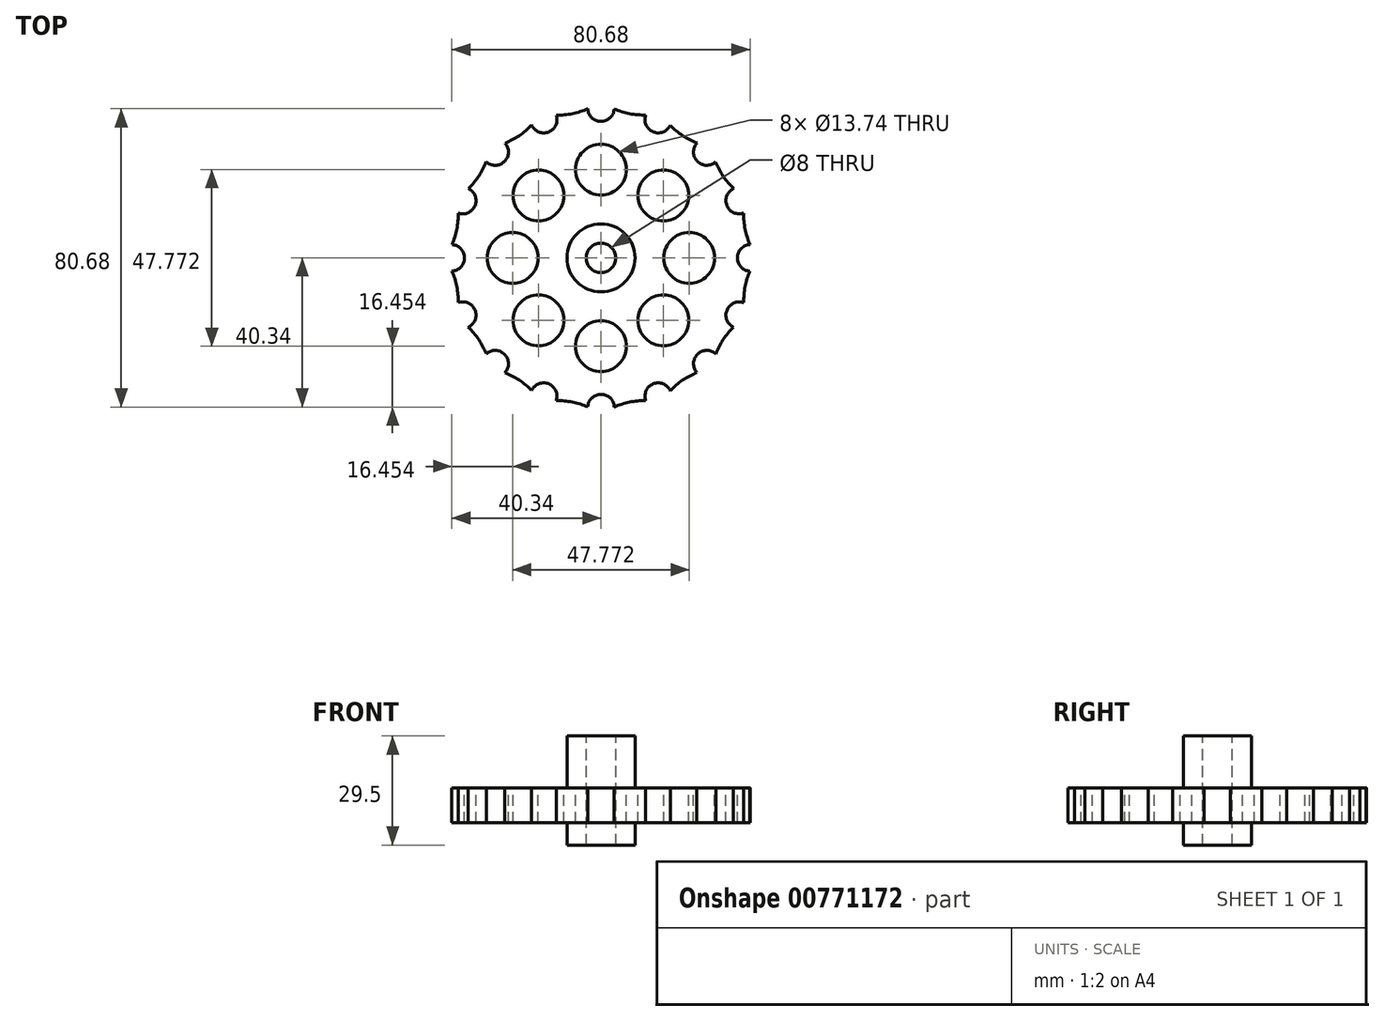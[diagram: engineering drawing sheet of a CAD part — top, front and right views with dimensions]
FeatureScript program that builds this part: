
annotation { "Feature Type Name" : "Feature", "Feature Type Description" : "" }
export const myFeature = defineFeature(function(context is Context, id is Id, definition is map)
    precondition{}
    {
        {
            var Q0;
            Q0=qCreatedBy(makeId("Front.planeOp"),FACE);
            var sketch = newSketch(context, id + "F0", { "sketchPlane" : qUnion([Q0])});
            skLineSegment(sketch, "E0", {"start": v(4, 29.5) * mm, "end": v(4, 0) * mm});
            skLineSegment(sketch, "E1", {"start": v(4, 0) * mm, "end": v(9.2, 0) * mm});
            skLineSegment(sketch, "E2", {"start": v(9.2, 0) * mm, "end": v(9.2, 6) * mm});
            skLineSegment(sketch, "E3", {"start": v(9.2, 6) * mm, "end": v(40.5, 6) * mm});
            skLineSegment(sketch, "E4", {"start": v(40.5, 6) * mm, "end": v(40.5, 15.5) * mm});
            skLineSegment(sketch, "E5", {"start": v(40.5, 15.5) * mm, "end": v(9.2, 15.5) * mm});
            skLineSegment(sketch, "E6", {"start": v(9.2, 15.5) * mm, "end": v(9.2, 29.5) * mm});
            skLineSegment(sketch, "E7", {"start": v(9.2, 29.5) * mm, "end": v(4, 29.5) * mm});
            skLineSegment(sketch, "E8", {"start": v(0, 75.26) * mm, "end": v(0, -74.89) * mm});
            skSolve(sketch);
        }
        {
            var Q0;
            Q0=makeQuery(id+"F0.imprint","IMPRINT",FACE,{"disambiguationData":[TD([[makeQuery(id+"F0.imprint","IMPRINT",EDGE,{"derivedFrom":sQuery(id+"F0.wireOp",EDGE,"E0")}),1.0]])]});
            var Q1;
            Q1=sQuery(id+"F0.wireOp",EDGE,"E8");
            revolve(context, id + "F1", {"surfaceOperationType" : NewSurfaceOperationType.NEW, "entities" : qUnion([Q0]), "axis" : qUnion([Q1]), "revolveType" : RevolveType.FULL});
        }
        {
            var Q0;
            Q0=makeQuery(id+"F1.opRevolve","SWEPT_FACE",FACE,{"disambiguationData":[OSD([sQuery(id+"F0.wireOp",EDGE,"E5")])]});
            var sketch = newSketch(context, id + "F2", { "sketchPlane" : qUnion([Q0])});
            skCircle(sketch, "E9", {"center": v(40.5, 0) * mm, "radius": 3.6 * mm});
            skCircle(sketch, "E10.1.0", {"center": v(37.42, 15.5) * mm, "radius": 3.6 * mm});
            skCircle(sketch, "E10.2.0", {"center": v(28.64, 28.64) * mm, "radius": 3.6 * mm});
            skCircle(sketch, "E10.3.0", {"center": v(15.5, 37.42) * mm, "radius": 3.6 * mm});
            skCircle(sketch, "E10.4.0", {"center": v(0, 40.5) * mm, "radius": 3.6 * mm});
            skCircle(sketch, "E10.5.0", {"center": v(-15.5, 37.42) * mm, "radius": 3.6 * mm});
            skCircle(sketch, "E10.6.0", {"center": v(-28.64, 28.64) * mm, "radius": 3.6 * mm});
            skCircle(sketch, "E10.7.0", {"center": v(-37.42, 15.5) * mm, "radius": 3.6 * mm});
            skCircle(sketch, "E10.8.0", {"center": v(-40.5, 0) * mm, "radius": 3.6 * mm});
            skCircle(sketch, "E10.9.0", {"center": v(-37.42, -15.5) * mm, "radius": 3.6 * mm});
            skCircle(sketch, "E10.10.0", {"center": v(-28.64, -28.64) * mm, "radius": 3.6 * mm});
            skCircle(sketch, "E10.11.0", {"center": v(-15.5, -37.42) * mm, "radius": 3.6 * mm});
            skCircle(sketch, "E10.12.0", {"center": v(0, -40.5) * mm, "radius": 3.6 * mm});
            skCircle(sketch, "E10.13.0", {"center": v(15.5, -37.42) * mm, "radius": 3.6 * mm});
            skCircle(sketch, "E10.14.0", {"center": v(28.64, -28.64) * mm, "radius": 3.6 * mm});
            skCircle(sketch, "E10.15.0", {"center": v(37.42, -15.5) * mm, "radius": 3.6 * mm});
            skPoint(sketch, "E10.center", {"position": v(0, 0) * mm});
            skArc(sketch, "E11", {"start": v(38.6, 12.1) * mm, "mid": v(39.02, 7.76) * mm, "end": v(40.34, 3.6) * mm});
            skArc(sketch, "E12.1.0", {"start": v(31.04, 25.96) * mm, "mid": v(33.08, 22.1) * mm, "end": v(35.9, 18.76) * mm});
            skArc(sketch, "E12.2.0", {"start": v(18.74, 35.86) * mm, "mid": v(22.1, 33.07) * mm, "end": v(25.98, 31.07) * mm});
            skArc(sketch, "E12.3.0", {"start": v(3.6, 40.3) * mm, "mid": v(7.77, 39.01) * mm, "end": v(12.11, 38.65) * mm});
            skArc(sketch, "E12.4.0", {"start": v(-12.1, 38.6) * mm, "mid": v(-7.76, 39.02) * mm, "end": v(-3.6, 40.34) * mm});
            skArc(sketch, "E12.5.0", {"start": v(-25.96, 31.04) * mm, "mid": v(-22.1, 33.08) * mm, "end": v(-18.76, 35.9) * mm});
            skArc(sketch, "E12.6.0", {"start": v(-35.86, 18.74) * mm, "mid": v(-33.07, 22.1) * mm, "end": v(-31.07, 25.98) * mm});
            skArc(sketch, "E12.7.0", {"start": v(-40.3, 3.6) * mm, "mid": v(-39.01, 7.77) * mm, "end": v(-38.65, 12.11) * mm});
            skArc(sketch, "E12.8.0", {"start": v(-38.6, -12.1) * mm, "mid": v(-39.02, -7.76) * mm, "end": v(-40.34, -3.6) * mm});
            skArc(sketch, "E12.9.0", {"start": v(-31.04, -25.96) * mm, "mid": v(-33.08, -22.1) * mm, "end": v(-35.9, -18.76) * mm});
            skArc(sketch, "E12.10.0", {"start": v(-18.74, -35.86) * mm, "mid": v(-22.1, -33.07) * mm, "end": v(-25.98, -31.07) * mm});
            skArc(sketch, "E12.11.0", {"start": v(-3.6, -40.3) * mm, "mid": v(-7.77, -39.01) * mm, "end": v(-12.11, -38.65) * mm});
            skArc(sketch, "E12.12.0", {"start": v(12.1, -38.6) * mm, "mid": v(7.76, -39.02) * mm, "end": v(3.6, -40.34) * mm});
            skArc(sketch, "E12.13.0", {"start": v(25.96, -31.04) * mm, "mid": v(22.1, -33.08) * mm, "end": v(18.76, -35.9) * mm});
            skArc(sketch, "E12.14.0", {"start": v(35.86, -18.74) * mm, "mid": v(33.07, -22.1) * mm, "end": v(31.07, -25.98) * mm});
            skArc(sketch, "E12.15.0", {"start": v(40.3, -3.6) * mm, "mid": v(39.01, -7.77) * mm, "end": v(38.65, -12.11) * mm});
            skSolve(sketch);
        }
        {
            var Q0;
            {var subQ0=sQuery(id+"F2.wireOp",EDGE,"E9");var subQ1=makeQuery(id+"F1.opRevolve","SWEPT_EDGE",EDGE,{"disambiguationData":[OSD([sQuery(id+"F0.wireOp",EDGE,"E4"),sQuery(id+"F0.wireOp",EDGE,"E5")])]});var subQ3=makeQuery(id+"F2.imprint","INTERSECT",VERTEX,{"derivedFrom":[subQ1,subQ0]});Q0=makeQuery(id+"F2.imprint","IMPRINT",FACE,{"disambiguationData":[TD([[makeQuery(id+"F2.imprint","IMPRINT",EDGE,{"disambiguationData":[TD([[subQ3,-1.0]])],"derivedFrom":subQ0}),1.0]])]});}
            var Q1;
            {var subQ0=sQuery(id+"F2.wireOp",EDGE,"E10.1.0");var subQ1=makeQuery(id+"F1.opRevolve","SWEPT_EDGE",EDGE,{"disambiguationData":[OSD([sQuery(id+"F0.wireOp",EDGE,"E4"),sQuery(id+"F0.wireOp",EDGE,"E5")])]});var subQ3=makeQuery(id+"F2.imprint","INTERSECT",VERTEX,{"derivedFrom":[subQ1,subQ0]});Q1=makeQuery(id+"F2.imprint","IMPRINT",FACE,{"disambiguationData":[TD([[makeQuery(id+"F2.imprint","IMPRINT",EDGE,{"disambiguationData":[TD([[subQ3,-1.0]])],"derivedFrom":subQ0}),1.0]])]});}
            var Q2;
            {var subQ0=sQuery(id+"F2.wireOp",EDGE,"E10.2.0");var subQ1=makeQuery(id+"F1.opRevolve","SWEPT_EDGE",EDGE,{"disambiguationData":[OSD([sQuery(id+"F0.wireOp",EDGE,"E4"),sQuery(id+"F0.wireOp",EDGE,"E5")])]});var subQ3=makeQuery(id+"F2.imprint","INTERSECT",VERTEX,{"derivedFrom":[subQ1,subQ0]});Q2=makeQuery(id+"F2.imprint","IMPRINT",FACE,{"disambiguationData":[TD([[makeQuery(id+"F2.imprint","IMPRINT",EDGE,{"disambiguationData":[TD([[subQ3,-1.0]])],"derivedFrom":subQ0}),1.0]])]});}
            var Q3;
            {var subQ0=sQuery(id+"F2.wireOp",EDGE,"E10.3.0");var subQ1=makeQuery(id+"F1.opRevolve","SWEPT_EDGE",EDGE,{"disambiguationData":[OSD([sQuery(id+"F0.wireOp",EDGE,"E4"),sQuery(id+"F0.wireOp",EDGE,"E5")])]});var subQ3=makeQuery(id+"F2.imprint","INTERSECT",VERTEX,{"derivedFrom":[subQ1,subQ0]});Q3=makeQuery(id+"F2.imprint","IMPRINT",FACE,{"disambiguationData":[TD([[makeQuery(id+"F2.imprint","IMPRINT",EDGE,{"disambiguationData":[TD([[subQ3,-1.0]])],"derivedFrom":subQ0}),1.0]])]});}
            var Q4;
            {var subQ0=sQuery(id+"F2.wireOp",EDGE,"E10.4.0");var subQ1=makeQuery(id+"F1.opRevolve","SWEPT_EDGE",EDGE,{"disambiguationData":[OSD([sQuery(id+"F0.wireOp",EDGE,"E4"),sQuery(id+"F0.wireOp",EDGE,"E5")])]});var subQ3=makeQuery(id+"F2.imprint","INTERSECT",VERTEX,{"derivedFrom":[subQ1,subQ0]});Q4=makeQuery(id+"F2.imprint","IMPRINT",FACE,{"disambiguationData":[TD([[makeQuery(id+"F2.imprint","IMPRINT",EDGE,{"disambiguationData":[TD([[subQ3,-1.0]])],"derivedFrom":subQ0}),1.0]])]});}
            var Q5;
            {var subQ0=sQuery(id+"F2.wireOp",EDGE,"E10.5.0");var subQ1=makeQuery(id+"F1.opRevolve","SWEPT_EDGE",EDGE,{"disambiguationData":[OSD([sQuery(id+"F0.wireOp",EDGE,"E4"),sQuery(id+"F0.wireOp",EDGE,"E5")])]});var subQ3=makeQuery(id+"F2.imprint","INTERSECT",VERTEX,{"derivedFrom":[subQ1,subQ0]});Q5=makeQuery(id+"F2.imprint","IMPRINT",FACE,{"disambiguationData":[TD([[makeQuery(id+"F2.imprint","IMPRINT",EDGE,{"disambiguationData":[TD([[subQ3,-1.0]])],"derivedFrom":subQ0}),1.0]])]});}
            var Q6;
            {var subQ0=sQuery(id+"F2.wireOp",EDGE,"E10.6.0");var subQ1=makeQuery(id+"F1.opRevolve","SWEPT_EDGE",EDGE,{"disambiguationData":[OSD([sQuery(id+"F0.wireOp",EDGE,"E4"),sQuery(id+"F0.wireOp",EDGE,"E5")])]});var subQ3=makeQuery(id+"F2.imprint","INTERSECT",VERTEX,{"derivedFrom":[subQ1,subQ0]});Q6=makeQuery(id+"F2.imprint","IMPRINT",FACE,{"disambiguationData":[TD([[makeQuery(id+"F2.imprint","IMPRINT",EDGE,{"disambiguationData":[TD([[subQ3,-1.0]])],"derivedFrom":subQ0}),1.0]])]});}
            var Q7;
            {var subQ0=sQuery(id+"F2.wireOp",EDGE,"E10.7.0");var subQ1=makeQuery(id+"F1.opRevolve","SWEPT_EDGE",EDGE,{"disambiguationData":[OSD([sQuery(id+"F0.wireOp",EDGE,"E4"),sQuery(id+"F0.wireOp",EDGE,"E5")])]});var subQ3=makeQuery(id+"F2.imprint","INTERSECT",VERTEX,{"derivedFrom":[subQ1,subQ0]});Q7=makeQuery(id+"F2.imprint","IMPRINT",FACE,{"disambiguationData":[TD([[makeQuery(id+"F2.imprint","IMPRINT",EDGE,{"disambiguationData":[TD([[subQ3,-1.0]])],"derivedFrom":subQ0}),1.0]])]});}
            var Q8;
            {var subQ0=sQuery(id+"F2.wireOp",EDGE,"E10.8.0");var subQ1=makeQuery(id+"F1.opRevolve","SWEPT_EDGE",EDGE,{"disambiguationData":[OSD([sQuery(id+"F0.wireOp",EDGE,"E4"),sQuery(id+"F0.wireOp",EDGE,"E5")])]});var subQ3=makeQuery(id+"F2.imprint","INTERSECT",VERTEX,{"derivedFrom":[subQ1,subQ0]});Q8=makeQuery(id+"F2.imprint","IMPRINT",FACE,{"disambiguationData":[TD([[makeQuery(id+"F2.imprint","IMPRINT",EDGE,{"disambiguationData":[TD([[subQ3,-1.0]])],"derivedFrom":subQ0}),1.0]])]});}
            var Q9;
            {var subQ0=sQuery(id+"F2.wireOp",EDGE,"E10.9.0");var subQ1=makeQuery(id+"F1.opRevolve","SWEPT_EDGE",EDGE,{"disambiguationData":[OSD([sQuery(id+"F0.wireOp",EDGE,"E4"),sQuery(id+"F0.wireOp",EDGE,"E5")])]});var subQ3=makeQuery(id+"F2.imprint","INTERSECT",VERTEX,{"derivedFrom":[subQ1,subQ0]});Q9=makeQuery(id+"F2.imprint","IMPRINT",FACE,{"disambiguationData":[TD([[makeQuery(id+"F2.imprint","IMPRINT",EDGE,{"disambiguationData":[TD([[subQ3,-1.0]])],"derivedFrom":subQ0}),1.0]])]});}
            var Q10;
            {var subQ0=sQuery(id+"F2.wireOp",EDGE,"E10.10.0");var subQ1=makeQuery(id+"F1.opRevolve","SWEPT_EDGE",EDGE,{"disambiguationData":[OSD([sQuery(id+"F0.wireOp",EDGE,"E4"),sQuery(id+"F0.wireOp",EDGE,"E5")])]});var subQ3=makeQuery(id+"F2.imprint","INTERSECT",VERTEX,{"derivedFrom":[subQ1,subQ0]});Q10=makeQuery(id+"F2.imprint","IMPRINT",FACE,{"disambiguationData":[TD([[makeQuery(id+"F2.imprint","IMPRINT",EDGE,{"disambiguationData":[TD([[subQ3,-1.0]])],"derivedFrom":subQ0}),1.0]])]});}
            var Q11;
            {var subQ0=sQuery(id+"F2.wireOp",EDGE,"E10.11.0");var subQ1=makeQuery(id+"F1.opRevolve","SWEPT_EDGE",EDGE,{"disambiguationData":[OSD([sQuery(id+"F0.wireOp",EDGE,"E4"),sQuery(id+"F0.wireOp",EDGE,"E5")])]});var subQ3=makeQuery(id+"F2.imprint","INTERSECT",VERTEX,{"derivedFrom":[subQ1,subQ0]});Q11=makeQuery(id+"F2.imprint","IMPRINT",FACE,{"disambiguationData":[TD([[makeQuery(id+"F2.imprint","IMPRINT",EDGE,{"disambiguationData":[TD([[subQ3,-1.0]])],"derivedFrom":subQ0}),1.0]])]});}
            var Q12;
            {var subQ0=sQuery(id+"F2.wireOp",EDGE,"E10.12.0");var subQ1=makeQuery(id+"F1.opRevolve","SWEPT_EDGE",EDGE,{"disambiguationData":[OSD([sQuery(id+"F0.wireOp",EDGE,"E4"),sQuery(id+"F0.wireOp",EDGE,"E5")])]});var subQ3=makeQuery(id+"F2.imprint","INTERSECT",VERTEX,{"derivedFrom":[subQ1,subQ0]});Q12=makeQuery(id+"F2.imprint","IMPRINT",FACE,{"disambiguationData":[TD([[makeQuery(id+"F2.imprint","IMPRINT",EDGE,{"disambiguationData":[TD([[subQ3,-1.0]])],"derivedFrom":subQ0}),1.0]])]});}
            var Q13;
            {var subQ0=sQuery(id+"F2.wireOp",EDGE,"E10.13.0");var subQ1=makeQuery(id+"F1.opRevolve","SWEPT_EDGE",EDGE,{"disambiguationData":[OSD([sQuery(id+"F0.wireOp",EDGE,"E4"),sQuery(id+"F0.wireOp",EDGE,"E5")])]});var subQ3=makeQuery(id+"F2.imprint","INTERSECT",VERTEX,{"derivedFrom":[subQ1,subQ0]});Q13=makeQuery(id+"F2.imprint","IMPRINT",FACE,{"disambiguationData":[TD([[makeQuery(id+"F2.imprint","IMPRINT",EDGE,{"disambiguationData":[TD([[subQ3,-1.0]])],"derivedFrom":subQ0}),1.0]])]});}
            var Q14;
            {var subQ0=sQuery(id+"F2.wireOp",EDGE,"E10.14.0");var subQ1=makeQuery(id+"F1.opRevolve","SWEPT_EDGE",EDGE,{"disambiguationData":[OSD([sQuery(id+"F0.wireOp",EDGE,"E4"),sQuery(id+"F0.wireOp",EDGE,"E5")])]});var subQ3=makeQuery(id+"F2.imprint","INTERSECT",VERTEX,{"derivedFrom":[subQ1,subQ0]});Q14=makeQuery(id+"F2.imprint","IMPRINT",FACE,{"disambiguationData":[TD([[makeQuery(id+"F2.imprint","IMPRINT",EDGE,{"disambiguationData":[TD([[subQ3,-1.0]])],"derivedFrom":subQ0}),1.0]])]});}
            var Q15;
            {var subQ0=sQuery(id+"F2.wireOp",EDGE,"E10.15.0");var subQ1=makeQuery(id+"F1.opRevolve","SWEPT_EDGE",EDGE,{"disambiguationData":[OSD([sQuery(id+"F0.wireOp",EDGE,"E4"),sQuery(id+"F0.wireOp",EDGE,"E5")])]});var subQ3=makeQuery(id+"F2.imprint","INTERSECT",VERTEX,{"derivedFrom":[subQ1,subQ0]});Q15=makeQuery(id+"F2.imprint","IMPRINT",FACE,{"disambiguationData":[TD([[makeQuery(id+"F2.imprint","IMPRINT",EDGE,{"disambiguationData":[TD([[subQ3,-1.0]])],"derivedFrom":subQ0}),1.0]])]});}
            var Q16;
            {var subQ0=sQuery(id+"F2.wireOp",EDGE,"E9");var subQ3=makeQuery(id+"F2.imprint","INTERSECT",VERTEX,{"derivedFrom":[subQ0,sQuery(id+"F2.wireOp",EDGE,"E12.15.0")]});Q16=makeQuery(id+"F2.imprint","IMPRINT",FACE,{"disambiguationData":[TD([[makeQuery(id+"F2.imprint","IMPRINT",EDGE,{"disambiguationData":[TD([[subQ3,-1.0]])],"derivedFrom":subQ0}),1.0]])]});}
            var Q17;
            {var subQ0=sQuery(id+"F2.wireOp",EDGE,"E10.1.0");var subQ1=makeQuery(id+"F2.imprint","INTERSECT",VERTEX,{"derivedFrom":[subQ0,sQuery(id+"F2.wireOp",EDGE,"E11")]});Q17=makeQuery(id+"F2.imprint","IMPRINT",FACE,{"disambiguationData":[TD([[makeQuery(id+"F2.imprint","IMPRINT",EDGE,{"disambiguationData":[TD([[subQ1,-1.0]])],"derivedFrom":subQ0}),1.0]])]});}
            var Q18;
            {var subQ0=sQuery(id+"F2.wireOp",EDGE,"E10.2.0");var subQ1=makeQuery(id+"F2.imprint","INTERSECT",VERTEX,{"derivedFrom":[subQ0,sQuery(id+"F2.wireOp",EDGE,"E12.1.0")]});Q18=makeQuery(id+"F2.imprint","IMPRINT",FACE,{"disambiguationData":[TD([[makeQuery(id+"F2.imprint","IMPRINT",EDGE,{"disambiguationData":[TD([[subQ1,-1.0]])],"derivedFrom":subQ0}),1.0]])]});}
            var Q19;
            {var subQ0=sQuery(id+"F2.wireOp",EDGE,"E10.3.0");var subQ1=makeQuery(id+"F2.imprint","INTERSECT",VERTEX,{"derivedFrom":[subQ0,sQuery(id+"F2.wireOp",EDGE,"E12.2.0")]});Q19=makeQuery(id+"F2.imprint","IMPRINT",FACE,{"disambiguationData":[TD([[makeQuery(id+"F2.imprint","IMPRINT",EDGE,{"disambiguationData":[TD([[subQ1,-1.0]])],"derivedFrom":subQ0}),1.0]])]});}
            var Q20;
            {var subQ0=sQuery(id+"F2.wireOp",EDGE,"E10.4.0");var subQ1=makeQuery(id+"F2.imprint","INTERSECT",VERTEX,{"derivedFrom":[subQ0,sQuery(id+"F2.wireOp",EDGE,"E12.3.0")]});Q20=makeQuery(id+"F2.imprint","IMPRINT",FACE,{"disambiguationData":[TD([[makeQuery(id+"F2.imprint","IMPRINT",EDGE,{"disambiguationData":[TD([[subQ1,-1.0]])],"derivedFrom":subQ0}),1.0]])]});}
            var Q21;
            {var subQ0=sQuery(id+"F2.wireOp",EDGE,"E10.5.0");var subQ1=makeQuery(id+"F2.imprint","INTERSECT",VERTEX,{"derivedFrom":[subQ0,sQuery(id+"F2.wireOp",EDGE,"E12.4.0")]});Q21=makeQuery(id+"F2.imprint","IMPRINT",FACE,{"disambiguationData":[TD([[makeQuery(id+"F2.imprint","IMPRINT",EDGE,{"disambiguationData":[TD([[subQ1,-1.0]])],"derivedFrom":subQ0}),1.0]])]});}
            var Q22;
            {var subQ0=sQuery(id+"F2.wireOp",EDGE,"E10.6.0");var subQ1=makeQuery(id+"F2.imprint","INTERSECT",VERTEX,{"derivedFrom":[subQ0,sQuery(id+"F2.wireOp",EDGE,"E12.5.0")]});Q22=makeQuery(id+"F2.imprint","IMPRINT",FACE,{"disambiguationData":[TD([[makeQuery(id+"F2.imprint","IMPRINT",EDGE,{"disambiguationData":[TD([[subQ1,-1.0]])],"derivedFrom":subQ0}),1.0]])]});}
            var Q23;
            {var subQ0=sQuery(id+"F2.wireOp",EDGE,"E10.7.0");var subQ1=makeQuery(id+"F2.imprint","INTERSECT",VERTEX,{"derivedFrom":[subQ0,sQuery(id+"F2.wireOp",EDGE,"E12.6.0")]});Q23=makeQuery(id+"F2.imprint","IMPRINT",FACE,{"disambiguationData":[TD([[makeQuery(id+"F2.imprint","IMPRINT",EDGE,{"disambiguationData":[TD([[subQ1,-1.0]])],"derivedFrom":subQ0}),1.0]])]});}
            var Q24;
            {var subQ0=sQuery(id+"F2.wireOp",EDGE,"E10.8.0");var subQ1=makeQuery(id+"F2.imprint","INTERSECT",VERTEX,{"derivedFrom":[subQ0,sQuery(id+"F2.wireOp",EDGE,"E12.7.0")]});Q24=makeQuery(id+"F2.imprint","IMPRINT",FACE,{"disambiguationData":[TD([[makeQuery(id+"F2.imprint","IMPRINT",EDGE,{"disambiguationData":[TD([[subQ1,-1.0]])],"derivedFrom":subQ0}),1.0]])]});}
            var Q25;
            {var subQ0=sQuery(id+"F2.wireOp",EDGE,"E10.9.0");var subQ1=makeQuery(id+"F2.imprint","INTERSECT",VERTEX,{"derivedFrom":[subQ0,sQuery(id+"F2.wireOp",EDGE,"E12.8.0")]});Q25=makeQuery(id+"F2.imprint","IMPRINT",FACE,{"disambiguationData":[TD([[makeQuery(id+"F2.imprint","IMPRINT",EDGE,{"disambiguationData":[TD([[subQ1,-1.0]])],"derivedFrom":subQ0}),1.0]])]});}
            var Q26;
            {var subQ0=sQuery(id+"F2.wireOp",EDGE,"E10.10.0");var subQ1=makeQuery(id+"F2.imprint","INTERSECT",VERTEX,{"derivedFrom":[subQ0,sQuery(id+"F2.wireOp",EDGE,"E12.9.0")]});Q26=makeQuery(id+"F2.imprint","IMPRINT",FACE,{"disambiguationData":[TD([[makeQuery(id+"F2.imprint","IMPRINT",EDGE,{"disambiguationData":[TD([[subQ1,-1.0]])],"derivedFrom":subQ0}),1.0]])]});}
            var Q27;
            {var subQ0=sQuery(id+"F2.wireOp",EDGE,"E10.11.0");var subQ1=makeQuery(id+"F2.imprint","INTERSECT",VERTEX,{"derivedFrom":[subQ0,sQuery(id+"F2.wireOp",EDGE,"E12.10.0")]});Q27=makeQuery(id+"F2.imprint","IMPRINT",FACE,{"disambiguationData":[TD([[makeQuery(id+"F2.imprint","IMPRINT",EDGE,{"disambiguationData":[TD([[subQ1,-1.0]])],"derivedFrom":subQ0}),1.0]])]});}
            var Q28;
            {var subQ0=sQuery(id+"F2.wireOp",EDGE,"E10.12.0");var subQ1=makeQuery(id+"F2.imprint","INTERSECT",VERTEX,{"derivedFrom":[subQ0,sQuery(id+"F2.wireOp",EDGE,"E12.11.0")]});Q28=makeQuery(id+"F2.imprint","IMPRINT",FACE,{"disambiguationData":[TD([[makeQuery(id+"F2.imprint","IMPRINT",EDGE,{"disambiguationData":[TD([[subQ1,-1.0]])],"derivedFrom":subQ0}),1.0]])]});}
            var Q29;
            {var subQ0=sQuery(id+"F2.wireOp",EDGE,"E10.13.0");var subQ1=makeQuery(id+"F2.imprint","INTERSECT",VERTEX,{"derivedFrom":[subQ0,sQuery(id+"F2.wireOp",EDGE,"E12.12.0")]});Q29=makeQuery(id+"F2.imprint","IMPRINT",FACE,{"disambiguationData":[TD([[makeQuery(id+"F2.imprint","IMPRINT",EDGE,{"disambiguationData":[TD([[subQ1,-1.0]])],"derivedFrom":subQ0}),1.0]])]});}
            var Q30;
            {var subQ0=sQuery(id+"F2.wireOp",EDGE,"E10.14.0");var subQ1=makeQuery(id+"F2.imprint","INTERSECT",VERTEX,{"derivedFrom":[subQ0,sQuery(id+"F2.wireOp",EDGE,"E12.13.0")]});Q30=makeQuery(id+"F2.imprint","IMPRINT",FACE,{"disambiguationData":[TD([[makeQuery(id+"F2.imprint","IMPRINT",EDGE,{"disambiguationData":[TD([[subQ1,-1.0]])],"derivedFrom":subQ0}),1.0]])]});}
            var Q31;
            {var subQ0=sQuery(id+"F2.wireOp",EDGE,"E10.15.0");var subQ1=makeQuery(id+"F2.imprint","INTERSECT",VERTEX,{"derivedFrom":[subQ0,sQuery(id+"F2.wireOp",EDGE,"E12.14.0")]});Q31=makeQuery(id+"F2.imprint","IMPRINT",FACE,{"disambiguationData":[TD([[makeQuery(id+"F2.imprint","IMPRINT",EDGE,{"disambiguationData":[TD([[subQ1,-1.0]])],"derivedFrom":subQ0}),1.0]])]});}
            var Q32;
            {var subQ0=sQuery(id+"F2.wireOp",EDGE,"E11");Q32=makeQuery(id+"F2.imprint","IMPRINT",FACE,{"disambiguationData":[TD([[makeQuery(id+"F2.imprint","IMPRINT",EDGE,{"derivedFrom":subQ0}),1.0]])]});}
            var Q33;
            {var subQ0=sQuery(id+"F2.wireOp",EDGE,"E12.1.0");Q33=makeQuery(id+"F2.imprint","IMPRINT",FACE,{"disambiguationData":[TD([[makeQuery(id+"F2.imprint","IMPRINT",EDGE,{"derivedFrom":subQ0}),1.0]])]});}
            var Q34;
            {var subQ0=sQuery(id+"F2.wireOp",EDGE,"E12.13.0");Q34=makeQuery(id+"F2.imprint","IMPRINT",FACE,{"disambiguationData":[TD([[makeQuery(id+"F2.imprint","IMPRINT",EDGE,{"derivedFrom":subQ0}),1.0]])]});}
            var Q35;
            {var subQ0=sQuery(id+"F2.wireOp",EDGE,"E12.2.0");Q35=makeQuery(id+"F2.imprint","IMPRINT",FACE,{"disambiguationData":[TD([[makeQuery(id+"F2.imprint","IMPRINT",EDGE,{"derivedFrom":subQ0}),1.0]])]});}
            var Q36;
            {var subQ0=sQuery(id+"F2.wireOp",EDGE,"E12.14.0");Q36=makeQuery(id+"F2.imprint","IMPRINT",FACE,{"disambiguationData":[TD([[makeQuery(id+"F2.imprint","IMPRINT",EDGE,{"derivedFrom":subQ0}),1.0]])]});}
            var Q37;
            {var subQ0=sQuery(id+"F2.wireOp",EDGE,"E12.15.0");Q37=makeQuery(id+"F2.imprint","IMPRINT",FACE,{"disambiguationData":[TD([[makeQuery(id+"F2.imprint","IMPRINT",EDGE,{"derivedFrom":subQ0}),1.0]])]});}
            var Q38;
            {var subQ0=sQuery(id+"F2.wireOp",EDGE,"E12.7.0");Q38=makeQuery(id+"F2.imprint","IMPRINT",FACE,{"disambiguationData":[TD([[makeQuery(id+"F2.imprint","IMPRINT",EDGE,{"derivedFrom":subQ0}),1.0]])]});}
            var Q39;
            {var subQ0=sQuery(id+"F2.wireOp",EDGE,"E12.8.0");Q39=makeQuery(id+"F2.imprint","IMPRINT",FACE,{"disambiguationData":[TD([[makeQuery(id+"F2.imprint","IMPRINT",EDGE,{"derivedFrom":subQ0}),1.0]])]});}
            var Q40;
            {var subQ0=sQuery(id+"F2.wireOp",EDGE,"E12.9.0");Q40=makeQuery(id+"F2.imprint","IMPRINT",FACE,{"disambiguationData":[TD([[makeQuery(id+"F2.imprint","IMPRINT",EDGE,{"derivedFrom":subQ0}),1.0]])]});}
            var Q41;
            {var subQ0=sQuery(id+"F2.wireOp",EDGE,"E12.6.0");Q41=makeQuery(id+"F2.imprint","IMPRINT",FACE,{"disambiguationData":[TD([[makeQuery(id+"F2.imprint","IMPRINT",EDGE,{"derivedFrom":subQ0}),1.0]])]});}
            var Q42;
            {var subQ0=sQuery(id+"F2.wireOp",EDGE,"E12.10.0");Q42=makeQuery(id+"F2.imprint","IMPRINT",FACE,{"disambiguationData":[TD([[makeQuery(id+"F2.imprint","IMPRINT",EDGE,{"derivedFrom":subQ0}),1.0]])]});}
            var Q43;
            {var subQ0=sQuery(id+"F2.wireOp",EDGE,"E12.5.0");Q43=makeQuery(id+"F2.imprint","IMPRINT",FACE,{"disambiguationData":[TD([[makeQuery(id+"F2.imprint","IMPRINT",EDGE,{"derivedFrom":subQ0}),1.0]])]});}
            var Q44;
            {var subQ0=sQuery(id+"F2.wireOp",EDGE,"E12.4.0");Q44=makeQuery(id+"F2.imprint","IMPRINT",FACE,{"disambiguationData":[TD([[makeQuery(id+"F2.imprint","IMPRINT",EDGE,{"derivedFrom":subQ0}),1.0]])]});}
            var Q45;
            {var subQ0=sQuery(id+"F2.wireOp",EDGE,"E12.11.0");Q45=makeQuery(id+"F2.imprint","IMPRINT",FACE,{"disambiguationData":[TD([[makeQuery(id+"F2.imprint","IMPRINT",EDGE,{"derivedFrom":subQ0}),1.0]])]});}
            var Q46;
            {var subQ0=sQuery(id+"F2.wireOp",EDGE,"E12.12.0");Q46=makeQuery(id+"F2.imprint","IMPRINT",FACE,{"disambiguationData":[TD([[makeQuery(id+"F2.imprint","IMPRINT",EDGE,{"derivedFrom":subQ0}),1.0]])]});}
            var Q47;
            {var subQ0=sQuery(id+"F2.wireOp",EDGE,"E12.3.0");Q47=makeQuery(id+"F2.imprint","IMPRINT",FACE,{"disambiguationData":[TD([[makeQuery(id+"F2.imprint","IMPRINT",EDGE,{"derivedFrom":subQ0}),1.0]])]});}
            extrude(context, id + "F3", {"entities" : qUnion([Q0, Q1, Q2, Q3, Q4, Q5, Q6, Q7, Q8, Q9, Q10, Q11, Q12, Q13, Q14, Q15, Q16, Q17, Q18, Q19, Q20, Q21, Q22, Q23, Q24, Q25, Q26, Q27, Q28, Q29, Q30, Q31, Q32, Q33, Q34, Q35, Q36, Q37, Q38, Q39, Q40, Q41, Q42, Q43, Q44, Q45, Q46, Q47]), "operationType" : NewBodyOperationType.REMOVE, "endBound" : BoundingType.THROUGH_ALL, "oppositeDirection" : true, "depth" : 25 * mm, "offsetDistance" : 25 * mm});
        }
        {
            var Q0;
            Q0=makeQuery(id+"F1.opRevolve","SWEPT_FACE",FACE,{"disambiguationData":[OSD([sQuery(id+"F0.wireOp",EDGE,"E5")])]});
            var sketch = newSketch(context, id + "F4", { "sketchPlane" : qUnion([Q0])});
            skCircle(sketch, "E13", {"center": v(0, 0) * mm, "radius": 23.89 * mm});
            skCircle(sketch, "E14", {"center": v(23.89, 0) * mm, "radius": 6.87 * mm});
            skCircle(sketch, "E15.1.0", {"center": v(16.89, 16.89) * mm, "radius": 6.87 * mm});
            skCircle(sketch, "E15.2.0", {"center": v(0, 23.89) * mm, "radius": 6.87 * mm});
            skCircle(sketch, "E15.3.0", {"center": v(-16.89, 16.89) * mm, "radius": 6.87 * mm});
            skCircle(sketch, "E15.4.0", {"center": v(-23.89, 0) * mm, "radius": 6.87 * mm});
            skCircle(sketch, "E15.5.0", {"center": v(-16.89, -16.89) * mm, "radius": 6.87 * mm});
            skCircle(sketch, "E15.6.0", {"center": v(0, -23.89) * mm, "radius": 6.87 * mm});
            skCircle(sketch, "E15.7.0", {"center": v(16.89, -16.89) * mm, "radius": 6.87 * mm});
            skSolve(sketch);
        }
        {
            var Q0;
            {var subQ0=sQuery(id+"F4.wireOp",EDGE,"E14");var subQ1=sQuery(id+"F4.wireOp",EDGE,"E13");var subQ2=makeQuery(id+"F4.imprint","INTERSECT",VERTEX,{"disambiguationData":[OD(0.0)],"derivedFrom":[subQ1,subQ0]});Q0=makeQuery(id+"F4.imprint","IMPRINT",FACE,{"disambiguationData":[TD([[makeQuery(id+"F4.imprint","IMPRINT",EDGE,{"disambiguationData":[TD([[subQ2,1.0]])],"derivedFrom":subQ1}),-1.0]])]});}
            var Q1;
            {var subQ0=sQuery(id+"F4.wireOp",EDGE,"E15.1.0");var subQ1=sQuery(id+"F4.wireOp",EDGE,"E13");var subQ2=makeQuery(id+"F4.imprint","INTERSECT",VERTEX,{"disambiguationData":[OD(0.0)],"derivedFrom":[subQ1,subQ0]});Q1=makeQuery(id+"F4.imprint","IMPRINT",FACE,{"disambiguationData":[TD([[makeQuery(id+"F4.imprint","IMPRINT",EDGE,{"disambiguationData":[TD([[subQ2,-1.0]])],"derivedFrom":subQ1}),-1.0]])]});}
            var Q2;
            {var subQ0=sQuery(id+"F4.wireOp",EDGE,"E15.1.0");var subQ1=sQuery(id+"F4.wireOp",EDGE,"E13");var subQ2=makeQuery(id+"F4.imprint","INTERSECT",VERTEX,{"disambiguationData":[OD(0.0)],"derivedFrom":[subQ1,subQ0]});Q2=makeQuery(id+"F4.imprint","IMPRINT",FACE,{"disambiguationData":[TD([[makeQuery(id+"F4.imprint","IMPRINT",EDGE,{"disambiguationData":[TD([[subQ2,-1.0]])],"derivedFrom":subQ1}),1.0]])]});}
            var Q3;
            {var subQ0=sQuery(id+"F4.wireOp",EDGE,"E15.2.0");var subQ1=sQuery(id+"F4.wireOp",EDGE,"E13");var subQ2=makeQuery(id+"F4.imprint","INTERSECT",VERTEX,{"disambiguationData":[OD(0.0)],"derivedFrom":[subQ1,subQ0]});Q3=makeQuery(id+"F4.imprint","IMPRINT",FACE,{"disambiguationData":[TD([[makeQuery(id+"F4.imprint","IMPRINT",EDGE,{"disambiguationData":[TD([[subQ2,-1.0]])],"derivedFrom":subQ1}),-1.0]])]});}
            var Q4;
            {var subQ0=sQuery(id+"F4.wireOp",EDGE,"E15.2.0");var subQ1=sQuery(id+"F4.wireOp",EDGE,"E13");var subQ2=makeQuery(id+"F4.imprint","INTERSECT",VERTEX,{"disambiguationData":[OD(0.0)],"derivedFrom":[subQ1,subQ0]});Q4=makeQuery(id+"F4.imprint","IMPRINT",FACE,{"disambiguationData":[TD([[makeQuery(id+"F4.imprint","IMPRINT",EDGE,{"disambiguationData":[TD([[subQ2,-1.0]])],"derivedFrom":subQ1}),1.0]])]});}
            var Q5;
            {var subQ0=sQuery(id+"F4.wireOp",EDGE,"E15.3.0");var subQ1=sQuery(id+"F4.wireOp",EDGE,"E13");var subQ2=makeQuery(id+"F4.imprint","INTERSECT",VERTEX,{"disambiguationData":[OD(0.0)],"derivedFrom":[subQ1,subQ0]});Q5=makeQuery(id+"F4.imprint","IMPRINT",FACE,{"disambiguationData":[TD([[makeQuery(id+"F4.imprint","IMPRINT",EDGE,{"disambiguationData":[TD([[subQ2,-1.0]])],"derivedFrom":subQ1}),1.0]])]});}
            var Q6;
            {var subQ0=sQuery(id+"F4.wireOp",EDGE,"E15.3.0");var subQ1=sQuery(id+"F4.wireOp",EDGE,"E13");var subQ2=makeQuery(id+"F4.imprint","INTERSECT",VERTEX,{"disambiguationData":[OD(0.0)],"derivedFrom":[subQ1,subQ0]});Q6=makeQuery(id+"F4.imprint","IMPRINT",FACE,{"disambiguationData":[TD([[makeQuery(id+"F4.imprint","IMPRINT",EDGE,{"disambiguationData":[TD([[subQ2,-1.0]])],"derivedFrom":subQ1}),-1.0]])]});}
            var Q7;
            {var subQ0=sQuery(id+"F4.wireOp",EDGE,"E15.4.0");var subQ1=sQuery(id+"F4.wireOp",EDGE,"E13");var subQ2=makeQuery(id+"F4.imprint","INTERSECT",VERTEX,{"disambiguationData":[OD(0.0)],"derivedFrom":[subQ1,subQ0]});Q7=makeQuery(id+"F4.imprint","IMPRINT",FACE,{"disambiguationData":[TD([[makeQuery(id+"F4.imprint","IMPRINT",EDGE,{"disambiguationData":[TD([[subQ2,-1.0]])],"derivedFrom":subQ1}),-1.0]])]});}
            var Q8;
            {var subQ0=sQuery(id+"F4.wireOp",EDGE,"E15.4.0");var subQ1=sQuery(id+"F4.wireOp",EDGE,"E13");var subQ2=makeQuery(id+"F4.imprint","INTERSECT",VERTEX,{"disambiguationData":[OD(0.0)],"derivedFrom":[subQ1,subQ0]});Q8=makeQuery(id+"F4.imprint","IMPRINT",FACE,{"disambiguationData":[TD([[makeQuery(id+"F4.imprint","IMPRINT",EDGE,{"disambiguationData":[TD([[subQ2,-1.0]])],"derivedFrom":subQ1}),1.0]])]});}
            var Q9;
            {var subQ0=sQuery(id+"F4.wireOp",EDGE,"E15.5.0");var subQ1=sQuery(id+"F4.wireOp",EDGE,"E13");var subQ2=makeQuery(id+"F4.imprint","INTERSECT",VERTEX,{"disambiguationData":[OD(0.0)],"derivedFrom":[subQ1,subQ0]});Q9=makeQuery(id+"F4.imprint","IMPRINT",FACE,{"disambiguationData":[TD([[makeQuery(id+"F4.imprint","IMPRINT",EDGE,{"disambiguationData":[TD([[subQ2,-1.0]])],"derivedFrom":subQ1}),-1.0]])]});}
            var Q10;
            {var subQ0=sQuery(id+"F4.wireOp",EDGE,"E15.5.0");var subQ1=sQuery(id+"F4.wireOp",EDGE,"E13");var subQ2=makeQuery(id+"F4.imprint","INTERSECT",VERTEX,{"disambiguationData":[OD(0.0)],"derivedFrom":[subQ1,subQ0]});Q10=makeQuery(id+"F4.imprint","IMPRINT",FACE,{"disambiguationData":[TD([[makeQuery(id+"F4.imprint","IMPRINT",EDGE,{"disambiguationData":[TD([[subQ2,-1.0]])],"derivedFrom":subQ1}),1.0]])]});}
            var Q11;
            {var subQ0=sQuery(id+"F4.wireOp",EDGE,"E15.6.0");var subQ1=sQuery(id+"F4.wireOp",EDGE,"E13");var subQ2=makeQuery(id+"F4.imprint","INTERSECT",VERTEX,{"disambiguationData":[OD(0.0)],"derivedFrom":[subQ1,subQ0]});Q11=makeQuery(id+"F4.imprint","IMPRINT",FACE,{"disambiguationData":[TD([[makeQuery(id+"F4.imprint","IMPRINT",EDGE,{"disambiguationData":[TD([[subQ2,-1.0]])],"derivedFrom":subQ1}),1.0]])]});}
            var Q12;
            {var subQ0=sQuery(id+"F4.wireOp",EDGE,"E15.6.0");var subQ1=sQuery(id+"F4.wireOp",EDGE,"E13");var subQ2=makeQuery(id+"F4.imprint","INTERSECT",VERTEX,{"disambiguationData":[OD(0.0)],"derivedFrom":[subQ1,subQ0]});Q12=makeQuery(id+"F4.imprint","IMPRINT",FACE,{"disambiguationData":[TD([[makeQuery(id+"F4.imprint","IMPRINT",EDGE,{"disambiguationData":[TD([[subQ2,-1.0]])],"derivedFrom":subQ1}),-1.0]])]});}
            var Q13;
            {var subQ0=sQuery(id+"F4.wireOp",EDGE,"E15.7.0");var subQ1=sQuery(id+"F4.wireOp",EDGE,"E13");var subQ2=makeQuery(id+"F4.imprint","INTERSECT",VERTEX,{"disambiguationData":[OD(0.0)],"derivedFrom":[subQ1,subQ0]});Q13=makeQuery(id+"F4.imprint","IMPRINT",FACE,{"disambiguationData":[TD([[makeQuery(id+"F4.imprint","IMPRINT",EDGE,{"disambiguationData":[TD([[subQ2,-1.0]])],"derivedFrom":subQ1}),1.0]])]});}
            var Q14;
            {var subQ0=sQuery(id+"F4.wireOp",EDGE,"E15.7.0");var subQ1=sQuery(id+"F4.wireOp",EDGE,"E13");var subQ2=makeQuery(id+"F4.imprint","INTERSECT",VERTEX,{"disambiguationData":[OD(0.0)],"derivedFrom":[subQ1,subQ0]});Q14=makeQuery(id+"F4.imprint","IMPRINT",FACE,{"disambiguationData":[TD([[makeQuery(id+"F4.imprint","IMPRINT",EDGE,{"disambiguationData":[TD([[subQ2,-1.0]])],"derivedFrom":subQ1}),-1.0]])]});}
            var Q15;
            {var subQ0=sQuery(id+"F4.wireOp",EDGE,"E14");var subQ1=sQuery(id+"F4.wireOp",EDGE,"E13");var subQ2=makeQuery(id+"F4.imprint","INTERSECT",VERTEX,{"disambiguationData":[OD(0.0)],"derivedFrom":[subQ1,subQ0]});Q15=makeQuery(id+"F4.imprint","IMPRINT",FACE,{"disambiguationData":[TD([[makeQuery(id+"F4.imprint","IMPRINT",EDGE,{"disambiguationData":[TD([[subQ2,1.0]])],"derivedFrom":subQ1}),1.0]])]});}
            extrude(context, id + "F5", {"entities" : qUnion([Q0, Q1, Q2, Q3, Q4, Q5, Q6, Q7, Q8, Q9, Q10, Q11, Q12, Q13, Q14, Q15]), "operationType" : NewBodyOperationType.REMOVE, "oppositeDirection" : true, "depth" : 25 * mm, "offsetDistance" : 25 * mm});
        }
    });
